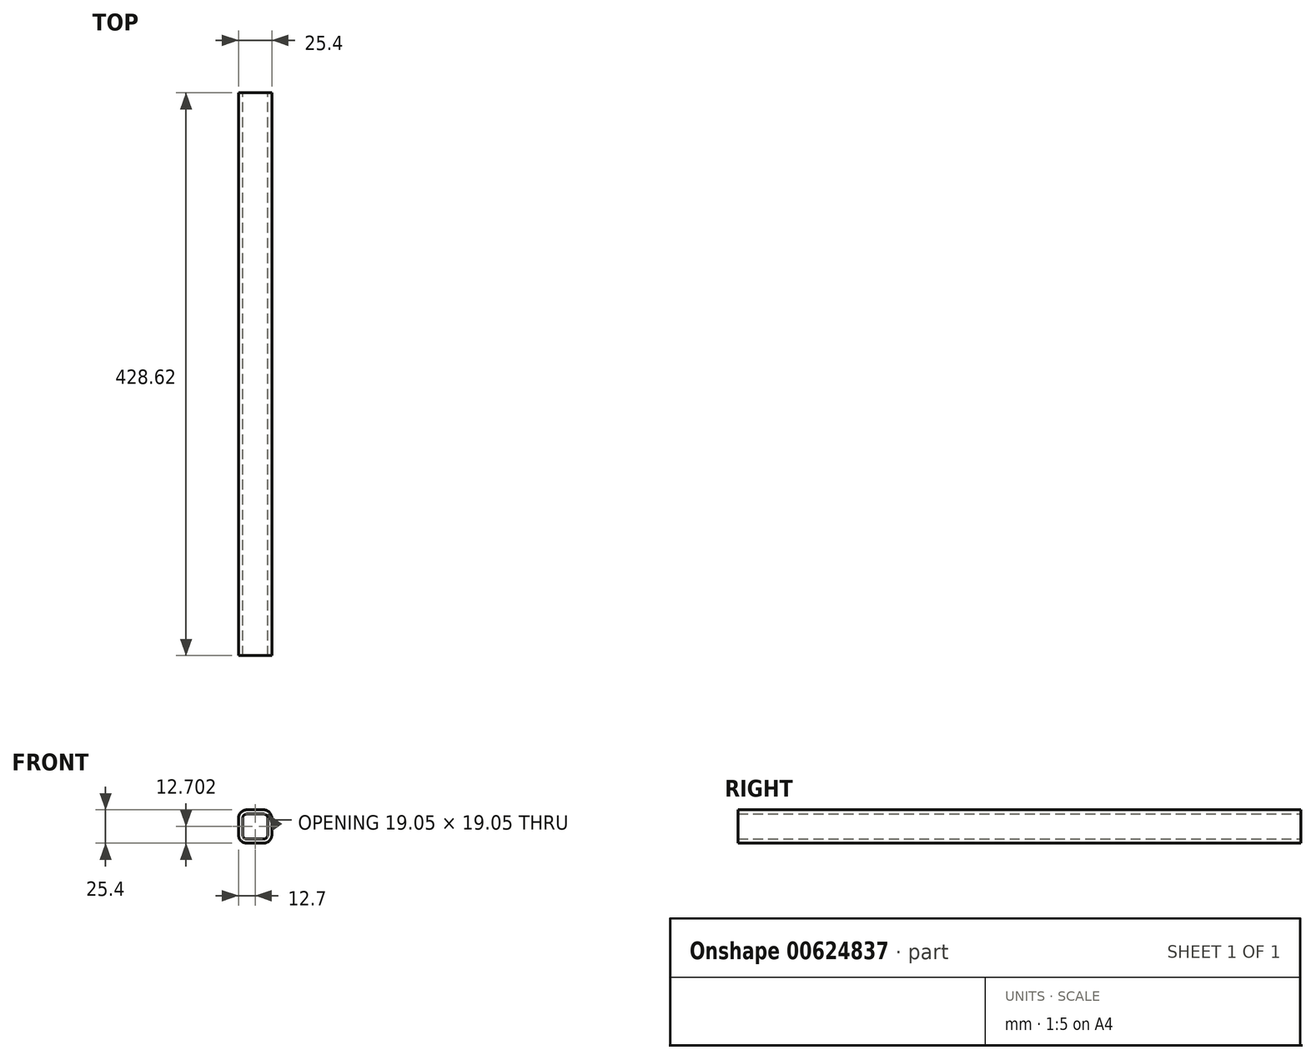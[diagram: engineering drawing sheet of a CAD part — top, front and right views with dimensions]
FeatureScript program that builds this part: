
annotation { "Feature Type Name" : "Feature", "Feature Type Description" : "" }
export const myFeature = defineFeature(function(context is Context, id is Id, definition is map)
    precondition{}
    {
        {
            var Q0;
            Q0=qCreatedBy(makeId("Front.planeOp"),FACE);
            var sketch = newSketch(context, id + "F0", { "sketchPlane" : qUnion([Q0])});
            skLineSegment(sketch, "E0.bottom", {"start": v(-6.35, 13.31) * mm, "end": v(6.35, 13.31) * mm});
            skLineSegment(sketch, "E0.top", {"start": v(-6.35, -12.09) * mm, "end": v(6.35, -12.09) * mm});
            skLineSegment(sketch, "E0.left", {"start": v(-12.7, 6.96) * mm, "end": v(-12.7, -5.74) * mm});
            skLineSegment(sketch, "E0.right", {"start": v(12.7, 6.96) * mm, "end": v(12.7, -5.74) * mm});
            skPoint(sketch, "E0.middle", {"position": v(0, 0.61) * mm});
            skPoint(sketch, "E1.visualSharp", {"position": v(-12.7, 13.31) * mm});
            skArc(sketch, "E1.filletArc", {"start": v(-11.77, 10.28) * mm, "mid": v(-12.46, 8.68) * mm, "end": v(-12.7, 6.96) * mm});
            skPoint(sketch, "E2.visualSharp", {"position": v(-6.35, 13.31) * mm});
            skArc(sketch, "E2.filletArc", {"start": v(-6.35, 13.31) * mm, "mid": v(-9.45, 12.5) * mm, "end": v(-11.77, 10.28) * mm});
            skPoint(sketch, "E3.visualSharp", {"position": v(12.7, 13.31) * mm});
            skArc(sketch, "E3.filletArc", {"start": v(12.7, 6.96) * mm, "mid": v(10.84, 11.45) * mm, "end": v(6.35, 13.31) * mm});
            skPoint(sketch, "E4.visualSharp", {"position": v(12.7, -12.09) * mm});
            skArc(sketch, "E4.filletArc", {"start": v(6.35, -12.09) * mm, "mid": v(10.84, -10.23) * mm, "end": v(12.7, -5.74) * mm});
            skPoint(sketch, "E5.visualSharp", {"position": v(-12.7, -12.09) * mm});
            skArc(sketch, "E5.filletArc", {"start": v(-12.7, -5.74) * mm, "mid": v(-10.84, -10.23) * mm, "end": v(-6.35, -12.09) * mm});
            skLineSegment(sketch, "E6.0", {"start": v(-9.52, 6.96) * mm, "end": v(-9.53, -5.74) * mm});
            skArc(sketch, "E6.1", {"start": v(-9.53, -5.74) * mm, "mid": v(-8.6, -7.98) * mm, "end": v(-6.35, -8.91) * mm});
            skLineSegment(sketch, "E6.2", {"start": v(-6.35, -8.91) * mm, "end": v(6.35, -8.91) * mm});
            skArc(sketch, "E6.3", {"start": v(6.35, -8.91) * mm, "mid": v(8.6, -7.98) * mm, "end": v(9.52, -5.74) * mm});
            skArc(sketch, "E6.4", {"start": v(-6.35, 10.14) * mm, "mid": v(-8.6, 9.2) * mm, "end": v(-9.52, 6.96) * mm});
            skLineSegment(sketch, "E6.5", {"start": v(-6.35, 10.14) * mm, "end": v(6.35, 10.14) * mm});
            skArc(sketch, "E6.6", {"start": v(9.53, 6.96) * mm, "mid": v(8.6, 9.2) * mm, "end": v(6.35, 10.14) * mm});
            skLineSegment(sketch, "E6.7", {"start": v(9.53, 6.96) * mm, "end": v(9.52, -5.74) * mm});
            skSolve(sketch);
        }
        {
            var Q0;
            Q0=qSketchRegion(id+"F0",true);
            extrude(context, id + "F1", {"entities" : qUnion([Q0]), "endBound" : BoundingType.SYMMETRIC, "depth" : 428.62 * mm, "offsetDistance" : 25.4 * mm});
        }
    });
